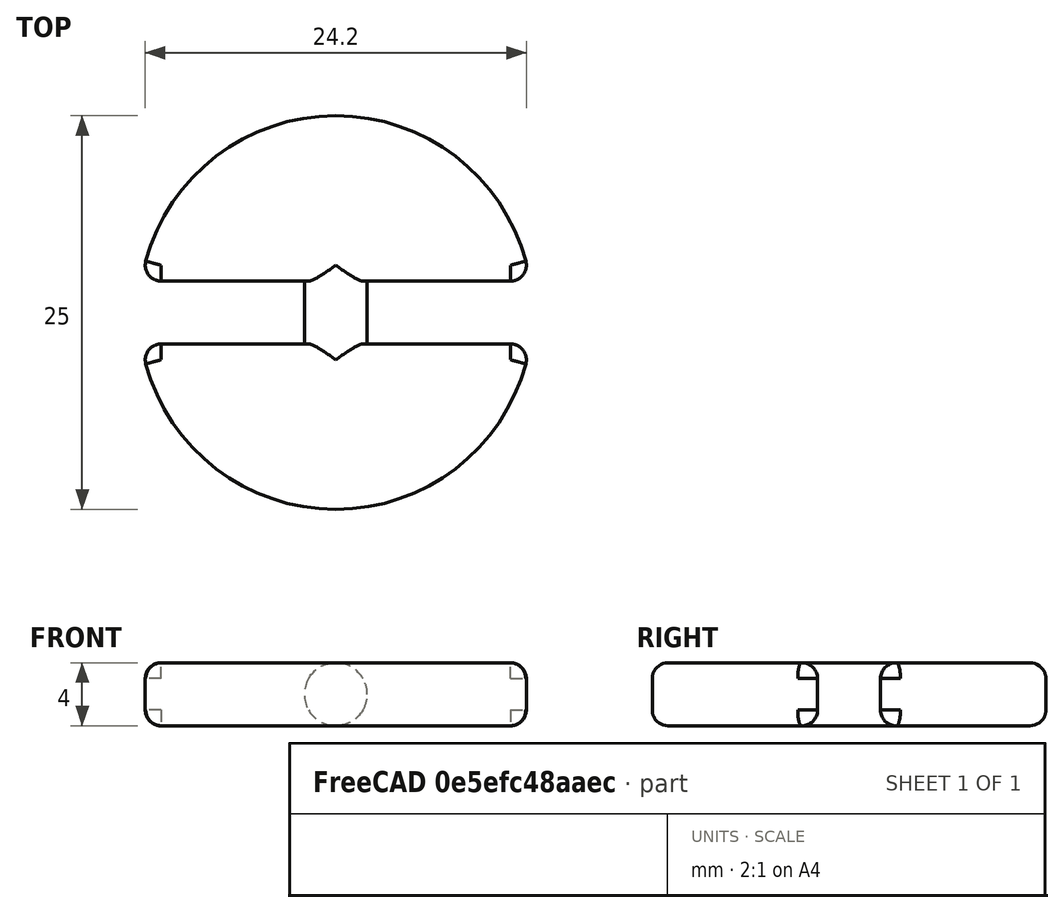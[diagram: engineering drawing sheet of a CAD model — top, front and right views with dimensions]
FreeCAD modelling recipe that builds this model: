
FCSTD DOCUMENT  (FreeCAD 0.16R6712 (Git))
Label: clip
License: All rights reserved
LicenseURL: http://en.wikipedia.org/wiki/All_rights_reserved
objects: PartDesign::Fillet×6, Part::Cylinder×2, Part::Box×1, Part::Cut×1, Part::MultiFuse×1
note: 11 computed .brp shape members not serialized (recipe doc carries the construction recipe); baked Part::Feature solids carry a one-line shape summary decoded from their .brp

FEATURE [Part::Cylinder] Cylinder
  Angle = 360
  Height = 10
  Placement = pos=(0,5,2) rot=(1,0,0;1.5708rad)
  Radius = 2
FEATURE [Part::Cylinder] Cylinder001
  Angle = 360
  Height = 4
  Radius = 12.5
FEATURE [Part::Box] Box  label="Cube"
  Height = 10
  Length = 25
  Placement = pos=(-12.5,-2,0) rot=(0,0,1;0rad)
  Width = 4
FEATURE [Part::Cut] Cut
  Base = -> Cylinder001
  Tool = -> Box
FEATURE [PartDesign::Fillet] Fillet
  Base = -> Cut [Edge4]
  Radius = 1
FEATURE [PartDesign::Fillet] Fillet001
  Base = -> Fillet [Edge3]
  Radius = 1
FEATURE [PartDesign::Fillet] Fillet002
  Base = -> Fillet001 [Edge13]
  Radius = 1
FEATURE [PartDesign::Fillet] Fillet003
  Base = -> Fillet002 [Edge3]
  Radius = 1
FEATURE [PartDesign::Fillet] Fillet004
  Base = -> Fillet003 [Edge8]
  Radius = 1
FEATURE [PartDesign::Fillet] Fillet005
  Base = -> Fillet004 [Edge36]
  Radius = 1
FEATURE [Part::MultiFuse] Fusion
  Shapes = -> [Cylinder,Fillet005]
